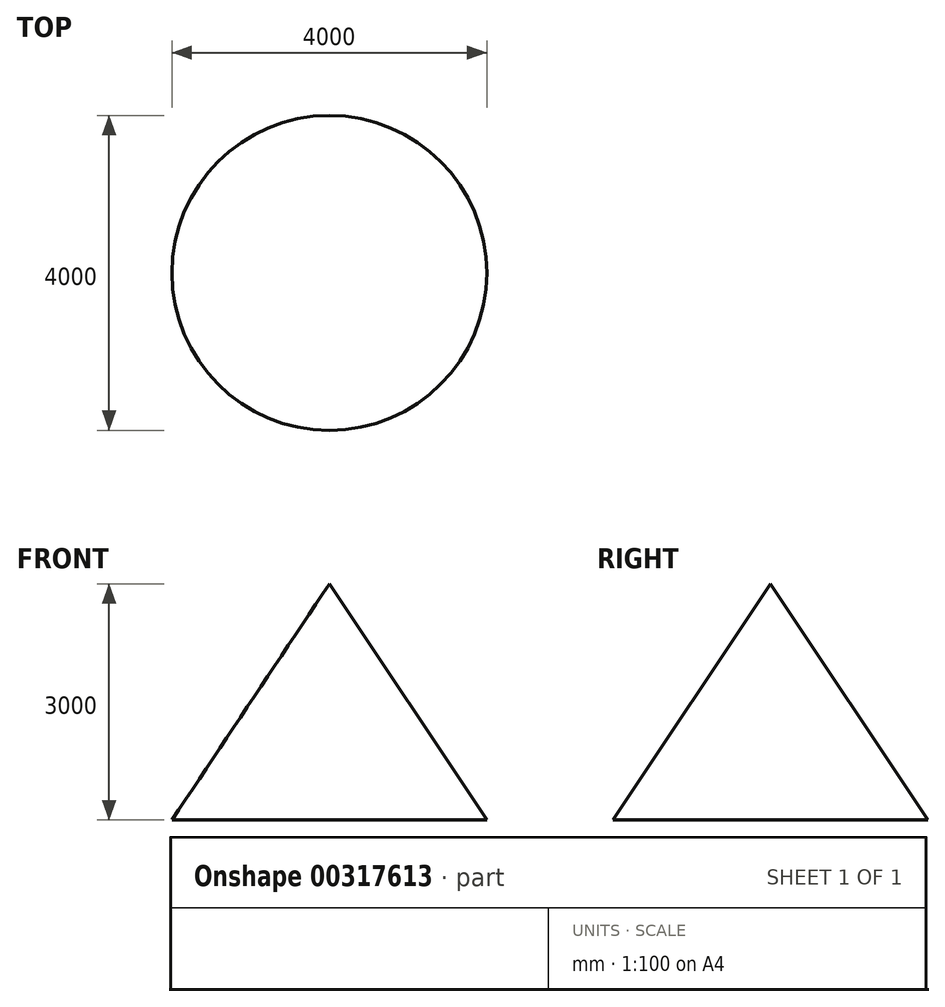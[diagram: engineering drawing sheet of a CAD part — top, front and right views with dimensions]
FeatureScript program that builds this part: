
annotation { "Feature Type Name" : "Feature", "Feature Type Description" : "" }
export const myFeature = defineFeature(function(context is Context, id is Id, definition is map)
    precondition{}
    {
        {
            var Q0;
            Q0=qCreatedBy(makeId("Front.planeOp"),FACE);
            var sketch = newSketch(context, id + "F0", { "sketchPlane" : qUnion([Q0])});
            skLineSegment(sketch, "E0", {"start": v(-21.25, 3000) * mm, "end": v(-21.25, 0) * mm});
            skLineSegment(sketch, "E1", {"start": v(-21.25, 3000) * mm, "end": v(1978.75, 0) * mm});
            skLineSegment(sketch, "E2", {"start": v(1978.75, 0) * mm, "end": v(-21.25, 0) * mm});
            skSolve(sketch);
        }
        {
            var Q0;
            Q0 = qSketchRegion(id + "F0", true);
            var Q1;
            Q1=sQuery(id+"F0.wireOp",EDGE,"E0");
            revolve(context, id + "F1", {"entities" : qUnion([Q0]), "axis" : qUnion([Q1]), "revolveType" : RevolveType.FULL});
        }
    });
